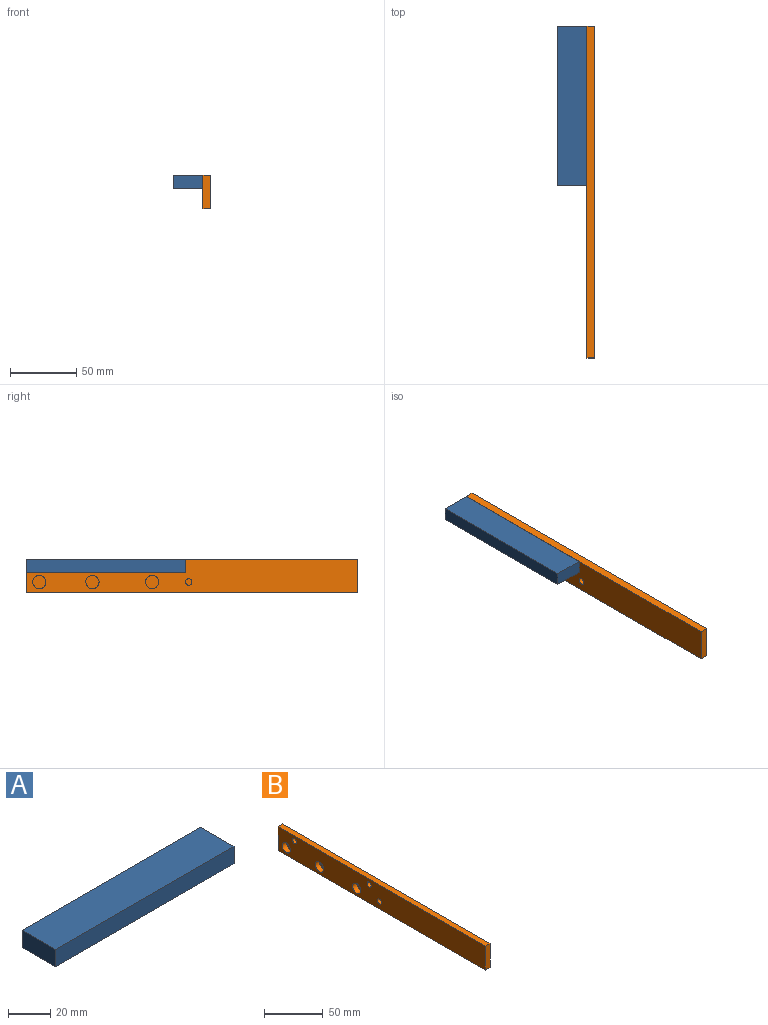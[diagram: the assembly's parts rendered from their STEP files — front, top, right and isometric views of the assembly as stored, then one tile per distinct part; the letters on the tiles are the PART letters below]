
ASSEMBLY  parts=2 mates=1
PART A: 16 faces, bbox 120x22.5x10 mm
  f0: plane 120x22.5mm, normal (0,0,-1), area 2464.4mm2, adj f1,f3,f4,f5,f6,f8,f10
  f1: plane 120x10mm, normal (0,1,0), area 1160.7mm2, adj f0,f2,f4,f5,f12,f14
  f2: plane 120x22.5mm, normal (0,0,1), area 2700mm2, adj f1,f3,f4,f5
  f3: plane 120x10mm, normal (0,-1,0), area 1200mm2, adj f0,f2,f4,f5
  f4: plane 22.5x10mm, normal (1,0,0), area 225mm2, adj f0,f1,f2,f3
  f5: plane 22.5x10mm, normal (-1,0,0), area 225mm2, adj f0,f1,f2,f3
  f6: cylinder r=5mm len=10mm, axis (0,0,-1), area 166.5mm2, adj f0,f7
  f7: plane 10x10mm, normal (0,0,-1), area 78.5mm2, adj f6
  f8: cylinder r=5mm len=10mm, axis (0,0,-1), area 166.5mm2, adj f0,f9
  f9: plane 10x10mm, normal (0,0,-1), area 78.5mm2, adj f8
  f10: cylinder r=5mm len=10mm, axis (0,0,-1), area 166.5mm2, adj f0,f11
  f11: plane 10x10mm, normal (0,0,-1), area 78.5mm2, adj f10
  f12: cylinder r=2.5mm len=10mm, axis (0,1,0), area 157.1mm2, adj f1,f13
  f13: plane 5x5mm, normal (0,1,0), area 19.6mm2, adj f12
  f14: cylinder r=2.5mm len=10mm, axis (0,1,0), area 157.1mm2, adj f1,f15
  f15: plane 5x5mm, normal (0,1,0), area 19.6mm2, adj f14
PART B: 18 faces, bbox 6x250x25 mm
  f0: plane 250x25mm, normal (1,0,0), area 6250mm2, adj f1,f3,f4,f5
  f1: plane 250x6mm, normal (0,0,1), area 1500mm2, adj f0,f2,f4,f5
  f2: plane 250x25mm, normal (-1,0,0), area 5955.5mm2, adj f1,f3,f4,f5,f6,f8,f10,f12
  f3: plane 250x6mm, normal (0,0,-1), area 1500mm2, adj f0,f2,f4,f5
  f4: plane 25x6mm, normal (0,-1,0), area 150mm2, adj f0,f1,f2,f3
  f5: plane 25x6mm, normal (0,1,0), area 150mm2, adj f0,f1,f2,f3
  f6: cylinder r=2.5mm len=5.3mm, axis (-1,0,0), area 83.3mm2, adj f2,f7
  f7: plane 5x5mm, normal (-1,0,0), area 19.6mm2, adj f6
  f8: cylinder r=5mm len=10mm, axis (-1,0,0), area 166.5mm2, adj f2,f9
  f9: plane 10x10mm, normal (-1,0,0), area 78.5mm2, adj f8
  f10: cylinder r=5mm len=10mm, axis (-1,0,0), area 166.5mm2, adj f2,f11
  f11: plane 10x10mm, normal (-1,0,0), area 78.5mm2, adj f10
  f12: cylinder r=5mm len=10mm, axis (-1,0,0), area 166.5mm2, adj f2,f13
  f13: plane 10x10mm, normal (-1,0,0), area 78.5mm2, adj f12
  f14: cylinder r=2.5mm len=5mm, axis (-1,0,0), area 78.5mm2, adj f2,f15
  f15: plane 5x5mm, normal (-1,0,0), area 19.6mm2, adj f14
  f16: cylinder r=2.5mm len=5mm, axis (-1,0,0), area 78.5mm2, adj f2,f17
  f17: plane 5x5mm, normal (-1,0,0), area 19.6mm2, adj f16
PLACE A rot(axis=(0,0,-1),90deg) t=(-3,0,2.38)mm
PLACE B at identity
MATE fastened A.f12 <-> B.f16  axis (1,0,0) through (-3,-20,7.38)mm
